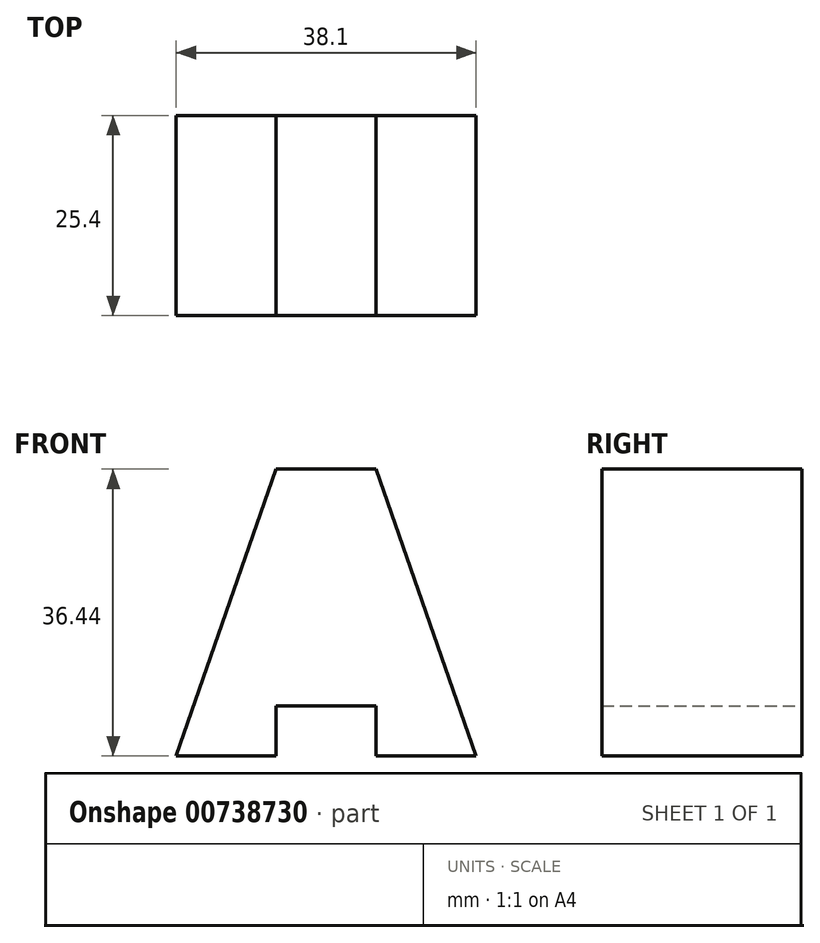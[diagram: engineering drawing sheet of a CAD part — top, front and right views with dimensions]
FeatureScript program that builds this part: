
annotation { "Feature Type Name" : "Feature", "Feature Type Description" : "" }
export const myFeature = defineFeature(function(context is Context, id is Id, definition is map)
    precondition{}
    {
        {
            var Q0;
            Q0=qCreatedBy(makeId("Front.planeOp"),FACE);
            var sketch = newSketch(context, id + "F0", { "sketchPlane" : qUnion([Q0])});
            skLineSegment(sketch, "E0", {"start": v(0, 0) * mm, "end": v(12.7, 0) * mm});
            skLineSegment(sketch, "E1", {"start": v(12.7, 0) * mm, "end": v(12.7, 6.35) * mm});
            skLineSegment(sketch, "E2", {"start": v(12.7, 6.35) * mm, "end": v(25.4, 6.35) * mm});
            skLineSegment(sketch, "E3", {"start": v(25.4, 6.35) * mm, "end": v(25.4, 0) * mm});
            skLineSegment(sketch, "E4", {"start": v(25.4, 0) * mm, "end": v(38.1, 0) * mm});
            skLineSegment(sketch, "E5", {"start": v(38.1, 0) * mm, "end": v(25.4, 36.44) * mm});
            skLineSegment(sketch, "E6", {"start": v(25.4, 36.44) * mm, "end": v(12.7, 36.44) * mm});
            skLineSegment(sketch, "E7", {"start": v(12.7, 36.44) * mm, "end": v(0, 0) * mm});
            skSolve(sketch);
        }
        {
            var Q0;
            Q0 = qSketchRegion(id + "F0", true);
            extrude(context, id + "F1", {"entities" : qUnion([Q0]), "depth" : 25.4 * mm, "offsetDistance" : 25.4 * mm});
        }
    });
